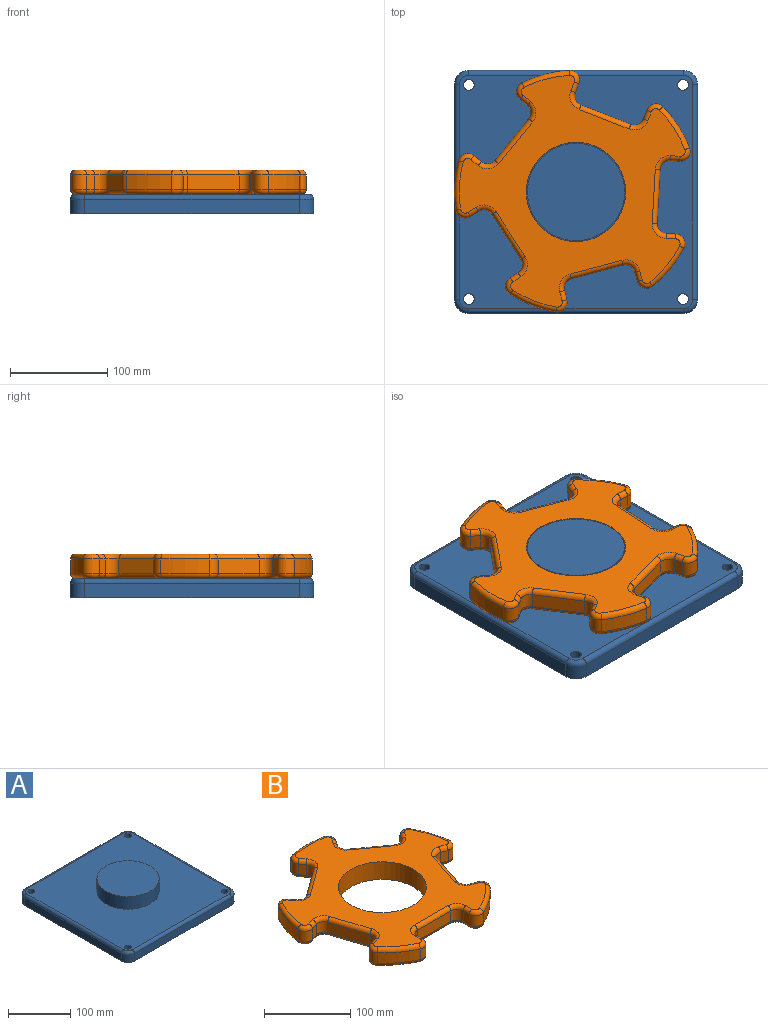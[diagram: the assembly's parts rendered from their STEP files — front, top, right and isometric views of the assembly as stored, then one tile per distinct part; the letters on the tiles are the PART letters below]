
ASSEMBLY  parts=2 mates=1
PART A: 24 faces, bbox 252.5x252.5x45 mm
  f0: plane 220x15mm, normal (1,0,0), area 3300mm2, adj f5,f8,f11,f19
  f1: plane 220x15mm, normal (0,1,0), area 3300mm2, adj f5,f8,f9,f23
  f2: plane 220x15mm, normal (-1,0,0), area 3300mm2, adj f5,f9,f10,f20
  f3: plane 220x15mm, normal (0,-1,0), area 3300mm2, adj f5,f10,f11,f16
  f4: plane 240x240mm, normal (0,0,1), area 49280mm2, adj f6,f12,f13,f14,f15,f16,f17,f18
  f5: plane 250x250mm, normal (0,0,-1), area 61926.7mm2, adj f0,f1,f2,f3,f8,f9,f10,f11
  f6: cylinder r=50mm len=100mm, axis (0,0,-1), area 7854mm2, adj f4,f7
  f7: plane 100x100mm, normal (0,0,1), area 7854mm2, adj f6
  f8: cylinder r=15mm len=15mm, axis (0,0,-1), area 353.4mm2, adj f0,f1,f5,f21
  f9: cylinder r=15mm len=15mm, axis (0,0,1), area 353.4mm2, adj f1,f2,f5,f22
  f10: cylinder r=15mm len=15mm, axis (0,0,-1), area 353.4mm2, adj f2,f3,f5,f18
  f11: cylinder r=15mm len=15mm, axis (0,0,1), area 353.4mm2, adj f0,f3,f5,f17
  f12: cylinder r=5.5mm len=20mm, axis (0,0,1), area 691.2mm2, adj f4,f5
  f13: cylinder r=5.5mm len=20mm, axis (0,0,1), area 691.2mm2, adj f4,f5
  f14: cylinder r=5.5mm len=20mm, axis (0,0,1), area 691.2mm2, adj f4,f5
  f15: cylinder r=5.5mm len=20mm, axis (0,0,1), area 691.2mm2, adj f4,f5
  f16: cylinder r=5mm len=220mm, axis (-1,0,0), area 1727.9mm2, adj f3,f4,f17,f18
  f17: torus R=10mm, axis (0,0,1), area 162.6mm2, adj f4,f11,f16,f19
  f18: torus R=10mm, axis (0,0,1), area 162.6mm2, adj f4,f10,f16,f20
  f19: cylinder r=5mm len=220mm, axis (0,-1,0), area 1727.9mm2, adj f0,f4,f17,f21
  f20: cylinder r=5mm len=220mm, axis (0,1,0), area 1727.9mm2, adj f2,f4,f18,f22
  f21: torus R=10mm, axis (0,0,1), area 162.6mm2, adj f4,f8,f19,f23
  f22: torus R=10mm, axis (0,0,1), area 162.6mm2, adj f4,f9,f20,f23
  f23: cylinder r=5mm len=220mm, axis (1,0,0), area 1727.9mm2, adj f1,f4,f21,f22
PART B: 123 faces, bbox 268.9x258.5x25 mm
  f0: plane 238.57x229.73mm, normal (0,0,1), area 21505.7mm2, adj f6,f43,f44,f45,f46,f47,f48,f49
  f1: plane 238.57x229.73mm, normal (0,0,-1), area 21505.7mm2, adj f6,f83,f84,f85,f86,f87,f88,f89
  f2: cylinder r=125mm len=40.68mm, axis (0,0,-1), area 759.5mm2, adj f13,f42,f51,f91
  f3: cylinder r=125mm len=47.82mm, axis (0,0,-1), area 759.5mm2, adj f35,f41,f67,f107
  f4: cylinder r=125mm len=50.29mm, axis (0,0,-1), area 759.5mm2, adj f28,f34,f82,f122
  f5: cylinder r=125mm len=47.82mm, axis (0,0,-1), area 759.5mm2, adj f21,f27,f66,f106
  f6: cylinder r=51mm len=102mm, axis (0,0,-1), area 8011.1mm2, adj f0,f1
  f7: cylinder r=125mm len=40.68mm, axis (0,0,-1), area 759.5mm2, adj f14,f20,f50,f90
  f8: plane 15x9.73mm, normal (-1,0,0), area 146mm2, adj f11,f14,f46,f86
  f9: plane 55x15mm, normal (0,-1,0), area 825mm2, adj f11,f12,f43,f83
  f10: plane 15x9.73mm, normal (1,0,0), area 146mm2, adj f12,f13,f47,f87
  f11: cylinder r=10mm len=15mm, axis (0,0,-1), area 235.6mm2, adj f8,f9,f44,f84
  f12: cylinder r=10mm len=15mm, axis (0,0,-1), area 235.6mm2, adj f9,f10,f45,f85
  f13: cylinder r=10mm len=15mm, axis (0,0,-1), area 299.5mm2, adj f2,f10,f49,f89
  f14: cylinder r=10mm len=15mm, axis (0,0,-1), area 299.5mm2, adj f7,f8,f48,f88
  f15: plane 15x9.26mm, normal (-0.31,-0.95,0), area 146mm2, adj f18,f21,f62,f102
  f16: plane 52.31x17mm, normal (0.95,-0.31,0), area 825mm2, adj f18,f19,f58,f98
  f17: plane 15x9.26mm, normal (0.31,0.95,0), area 146mm2, adj f19,f20,f54,f94
  f18: cylinder r=10mm len=15mm, axis (0,0,-1), area 235.6mm2, adj f15,f16,f60,f100
  f19: cylinder r=10mm len=15mm, axis (0,0,-1), area 235.6mm2, adj f16,f17,f56,f96
  f20: cylinder r=10mm len=16.25mm, axis (0,0,-1), area 299.5mm2, adj f7,f17,f52,f92
  f21: cylinder r=10mm len=15mm, axis (0,0,-1), area 299.5mm2, adj f5,f15,f64,f104
  f22: plane 15x7.87mm, normal (0.81,-0.59,0), area 146mm2, adj f25,f28,f78,f118
  f23: plane 44.5x32.33mm, normal (0.59,0.81,0), area 825mm2, adj f25,f26,f74,f114
  f24: plane 15x7.87mm, normal (-0.81,0.59,0), area 146mm2, adj f26,f27,f70,f110
  f25: cylinder r=10mm len=15mm, axis (0,0,-1), area 235.6mm2, adj f22,f23,f76,f116
  f26: cylinder r=10mm len=15mm, axis (0,0,-1), area 235.6mm2, adj f23,f24,f72,f112
  f27: cylinder r=10mm len=16.78mm, axis (0,0,-1), area 299.5mm2, adj f5,f24,f68,f108
  f28: cylinder r=10mm len=15.67mm, axis (0,0,-1), area 299.5mm2, adj f4,f22,f80,f120
  f29: plane 15x7.87mm, normal (0.81,0.59,0), area 146mm2, adj f32,f35,f71,f111
  f30: plane 44.5x32.33mm, normal (-0.59,0.81,0), area 825mm2, adj f32,f33,f75,f115
  f31: plane 15x7.87mm, normal (-0.81,-0.59,0), area 146mm2, adj f33,f34,f79,f119
  f32: cylinder r=10mm len=15mm, axis (0,0,-1), area 235.6mm2, adj f29,f30,f73,f113
  f33: cylinder r=10mm len=15mm, axis (0,0,-1), area 235.6mm2, adj f30,f31,f77,f117
  f34: cylinder r=10mm len=15.67mm, axis (0,0,-1), area 299.5mm2, adj f4,f31,f81,f121
  f35: cylinder r=10mm len=16.78mm, axis (0,0,-1), area 299.5mm2, adj f3,f29,f69,f109
  f36: plane 15x9.26mm, normal (-0.31,0.95,0), area 146mm2, adj f39,f42,f55,f95
  f37: plane 52.31x17mm, normal (-0.95,-0.31,0), area 825mm2, adj f39,f40,f59,f99
  f38: plane 15x9.26mm, normal (0.31,-0.95,0), area 146mm2, adj f40,f41,f63,f103
  f39: cylinder r=10mm len=15mm, axis (0,0,-1), area 235.6mm2, adj f36,f37,f57,f97
  f40: cylinder r=10mm len=15mm, axis (0,0,-1), area 235.6mm2, adj f37,f38,f61,f101
  f41: cylinder r=10mm len=15mm, axis (0,0,-1), area 299.5mm2, adj f3,f38,f65,f105
  f42: cylinder r=10mm len=16.25mm, axis (0,0,-1), area 299.5mm2, adj f2,f36,f53,f93
  f43: cylinder r=5mm len=55mm, axis (1,0,0), area 432mm2, adj f0,f9,f44,f45
  f44: torus R=15mm, axis (0,0,1), area 145.8mm2, adj f0,f11,f43,f46
  f45: torus R=15mm, axis (0,0,1), area 145.8mm2, adj f0,f12,f43,f47
  f46: cylinder r=5mm len=9.73mm, axis (0,-1,0), area 76.4mm2, adj f0,f8,f44,f48
  f47: cylinder r=5mm len=9.73mm, axis (0,1,0), area 76.4mm2, adj f0,f10,f45,f49
  f48: torus R=5mm, axis (0,0,1), area 128.3mm2, adj f0,f14,f46,f50
  f49: torus R=5mm, axis (0,0,1), area 128.3mm2, adj f0,f13,f47,f51
  f50: torus R=120mm, axis (0,0,1), area 391.9mm2, adj f0,f7,f48,f52
  f51: torus R=120mm, axis (0,0,1), area 391.9mm2, adj f0,f2,f49,f53
  f52: torus R=5mm, axis (0,0,1), area 128.3mm2, adj f0,f20,f50,f54
  f53: torus R=5mm, axis (0,0,1), area 128.3mm2, adj f0,f42,f51,f55
  f54: cylinder r=5mm len=10.8mm, axis (-0.95,0.31,0), area 76.4mm2, adj f0,f17,f52,f56
  f55: cylinder r=5mm len=10.8mm, axis (-0.95,-0.31,0), area 76.4mm2, adj f0,f36,f53,f57
  f56: torus R=15mm, axis (0,0,1), area 145.8mm2, adj f0,f19,f54,f58
  f57: torus R=15mm, axis (0,0,1), area 145.8mm2, adj f0,f39,f55,f59
  f58: cylinder r=5mm len=53.85mm, axis (0.31,0.95,0), area 432mm2, adj f0,f16,f56,f60
  f59: cylinder r=5mm len=53.85mm, axis (0.31,-0.95,0), area 432mm2, adj f0,f37,f57,f61
  f60: torus R=15mm, axis (0,0,1), area 145.8mm2, adj f0,f18,f58,f62
  f61: torus R=15mm, axis (0,0,1), area 145.8mm2, adj f0,f40,f59,f63
  f62: cylinder r=5mm len=10.8mm, axis (0.95,-0.31,0), area 76.4mm2, adj f0,f15,f60,f64
  f63: cylinder r=5mm len=10.8mm, axis (0.95,0.31,0), area 76.4mm2, adj f0,f38,f61,f65
  f64: torus R=5mm, axis (0,0,1), area 128.3mm2, adj f0,f21,f62,f66
  f65: torus R=5mm, axis (0,0,1), area 128.3mm2, adj f0,f41,f63,f67
  f66: torus R=120mm, axis (0,0,1), area 391.9mm2, adj f0,f5,f64,f68
  f67: torus R=120mm, axis (0,0,1), area 391.9mm2, adj f0,f3,f65,f69
  f68: torus R=5mm, axis (0,0,1), area 128.3mm2, adj f0,f27,f66,f70
  f69: torus R=5mm, axis (0,0,1), area 128.3mm2, adj f0,f35,f67,f71
  f70: cylinder r=5mm len=10.81mm, axis (-0.59,-0.81,0), area 76.4mm2, adj f0,f24,f68,f72
  f71: cylinder r=5mm len=10.81mm, axis (-0.59,0.81,0), area 76.4mm2, adj f0,f29,f69,f73
  f72: torus R=15mm, axis (0,0,1), area 145.8mm2, adj f0,f26,f70,f74
  f73: torus R=15mm, axis (0,0,1), area 145.8mm2, adj f0,f32,f71,f75
  f74: cylinder r=5mm len=47.44mm, axis (-0.81,0.59,0), area 432mm2, adj f0,f23,f72,f76
  f75: cylinder r=5mm len=47.44mm, axis (-0.81,-0.59,0), area 432mm2, adj f0,f30,f73,f77
  f76: torus R=15mm, axis (0,0,1), area 145.8mm2, adj f0,f25,f74,f78
  f77: torus R=15mm, axis (0,0,1), area 145.8mm2, adj f0,f33,f75,f79
  f78: cylinder r=5mm len=10.81mm, axis (0.59,0.81,0), area 76.4mm2, adj f0,f22,f76,f80
  f79: cylinder r=5mm len=10.81mm, axis (0.59,-0.81,0), area 76.4mm2, adj f0,f31,f77,f81
  f80: torus R=5mm, axis (0,0,1), area 128.3mm2, adj f0,f28,f78,f82
  f81: torus R=5mm, axis (0,0,1), area 128.3mm2, adj f0,f34,f79,f82
  f82: torus R=120mm, axis (0,0,1), area 391.9mm2, adj f0,f4,f80,f81
  f83: cylinder r=5mm len=55mm, axis (-1,0,0), area 432mm2, adj f1,f9,f84,f85
  f84: torus R=15mm, axis (0,0,1), area 145.8mm2, adj f1,f11,f83,f86
  f85: torus R=15mm, axis (0,0,1), area 145.8mm2, adj f1,f12,f83,f87
  f86: cylinder r=5mm len=9.73mm, axis (0,1,0), area 76.4mm2, adj f1,f8,f84,f88
  f87: cylinder r=5mm len=9.73mm, axis (0,-1,0), area 76.4mm2, adj f1,f10,f85,f89
  f88: torus R=5mm, axis (0,0,1), area 128.3mm2, adj f1,f14,f86,f90
  f89: torus R=5mm, axis (0,0,1), area 128.3mm2, adj f1,f13,f87,f91
  f90: torus R=120mm, axis (0,0,1), area 391.9mm2, adj f1,f7,f88,f92
  f91: torus R=120mm, axis (0,0,1), area 391.9mm2, adj f1,f2,f89,f93
  f92: torus R=5mm, axis (0,0,1), area 128.3mm2, adj f1,f20,f90,f94
  f93: torus R=5mm, axis (0,0,1), area 128.3mm2, adj f1,f42,f91,f95
  f94: cylinder r=5mm len=10.8mm, axis (0.95,-0.31,0), area 76.4mm2, adj f1,f17,f92,f96
  f95: cylinder r=5mm len=10.8mm, axis (0.95,0.31,0), area 76.4mm2, adj f1,f36,f93,f97
  f96: torus R=15mm, axis (0,0,1), area 145.8mm2, adj f1,f19,f94,f98
  f97: torus R=15mm, axis (0,0,1), area 145.8mm2, adj f1,f39,f95,f99
  f98: cylinder r=5mm len=53.85mm, axis (-0.31,-0.95,0), area 432mm2, adj f1,f16,f96,f100
  f99: cylinder r=5mm len=53.85mm, axis (-0.31,0.95,0), area 432mm2, adj f1,f37,f97,f101
  f100: torus R=15mm, axis (0,0,1), area 145.8mm2, adj f1,f18,f98,f102
  f101: torus R=15mm, axis (0,0,1), area 145.8mm2, adj f1,f40,f99,f103
  f102: cylinder r=5mm len=10.8mm, axis (-0.95,0.31,0), area 76.4mm2, adj f1,f15,f100,f104
  f103: cylinder r=5mm len=10.8mm, axis (-0.95,-0.31,0), area 76.4mm2, adj f1,f38,f101,f105
  f104: torus R=5mm, axis (0,0,1), area 128.3mm2, adj f1,f21,f102,f106
  f105: torus R=5mm, axis (0,0,1), area 128.3mm2, adj f1,f41,f103,f107
  f106: torus R=120mm, axis (0,0,1), area 391.9mm2, adj f1,f5,f104,f108
  f107: torus R=120mm, axis (0,0,1), area 391.9mm2, adj f1,f3,f105,f109
  f108: torus R=5mm, axis (0,0,1), area 128.3mm2, adj f1,f27,f106,f110
  f109: torus R=5mm, axis (0,0,1), area 128.3mm2, adj f1,f35,f107,f111
  f110: cylinder r=5mm len=10.81mm, axis (0.59,0.81,0), area 76.4mm2, adj f1,f24,f108,f112
  f111: cylinder r=5mm len=10.81mm, axis (0.59,-0.81,0), area 76.4mm2, adj f1,f29,f109,f113
  f112: torus R=15mm, axis (0,0,1), area 145.8mm2, adj f1,f26,f110,f114
  f113: torus R=15mm, axis (0,0,1), area 145.8mm2, adj f1,f32,f111,f115
  f114: cylinder r=5mm len=47.44mm, axis (0.81,-0.59,0), area 432mm2, adj f1,f23,f112,f116
  f115: cylinder r=5mm len=47.44mm, axis (0.81,0.59,0), area 432mm2, adj f1,f30,f113,f117
  f116: torus R=15mm, axis (0,0,1), area 145.8mm2, adj f1,f25,f114,f118
  f117: torus R=15mm, axis (0,0,1), area 145.8mm2, adj f1,f33,f115,f119
  f118: cylinder r=5mm len=10.81mm, axis (-0.59,-0.81,0), area 76.4mm2, adj f1,f22,f116,f120
  f119: cylinder r=5mm len=10.81mm, axis (-0.59,0.81,0), area 76.4mm2, adj f1,f31,f117,f121
  f120: torus R=5mm, axis (0,0,1), area 128.3mm2, adj f1,f28,f118,f122
  f121: torus R=5mm, axis (0,0,1), area 128.3mm2, adj f1,f34,f119,f122
  f122: torus R=120mm, axis (0,0,1), area 391.9mm2, adj f1,f4,f120,f121
PLACE A t=(-84.36,-33.49,0.33)mm fixed
PLACE B rot(axis=(0,0,1),158.8deg) t=(-84.36,-33.49,0.33)mm
MATE revolute B.f2 <-> A.f6  axis (0,0,1) through (-84.36,-33.49,45.33)mm
